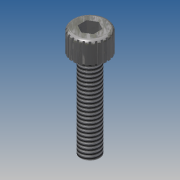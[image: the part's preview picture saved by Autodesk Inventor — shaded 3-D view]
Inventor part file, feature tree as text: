
AUTODESK INVENTOR PART (.ipt)
format: ipt  version: 2014 SP1 (Build 180222100, 222)  size: 246,272 bytes
history: native  units: in
note: dims shown in document units (in); Inventor stores cm internally (conversion verified against a paired STEP export)
features: sketch x5, extrude x4, fillet x1, thread x1, plane x1, pattern_circular x1
ambient origin geometry x8: Origin, YZ Plane, XZ Plane, XY Plane, X Axis, Y Axis, Z Axis, Center Point
bodies: Solid1 (feature_tree)
feature tree (13):
  extrude  "Extrusion1"  Depth=0.18in TaperAngle=0.0deg
  extrude  "Extrusion2"  Depth=0.03in
  fillet  "Fillet1"  Radius=0.162in
  extrude  "Extrusion3"  Depth=0.015in TaperAngle=0.0deg
  thread  "Thread3"  [1 undecoded]
  sketch  "Sketch4"  dims[d16=0.01in d17=0.0in d18=9.4488in d19=360.0deg]
  plane  "Work Plane1"
  extrude  "Extrusion4"  Depth=9.4488in TaperAngle=360.0deg
  pattern_circular  "Circular Pattern1"  [2 undecoded]
  sketch  "Sketch1"  dims[d0=0.3in d1=0.18in d2=0.0in]
  sketch  "Sketch2"  dims[d3=0.1in d4=0.0in d5=0.03in d6=0.162in]
  sketch  "Sketch3"  dims[d7=0.75in d8=0.0in d13=1.0in d14=0.0in d15=0.015in]
  sketch  "Sketch5"
note: 3 required parameter values undecoded (feature->parameter linkage not recoverable at this tier; creation-order binding heuristic only, values carry confidence <= 0.55)
